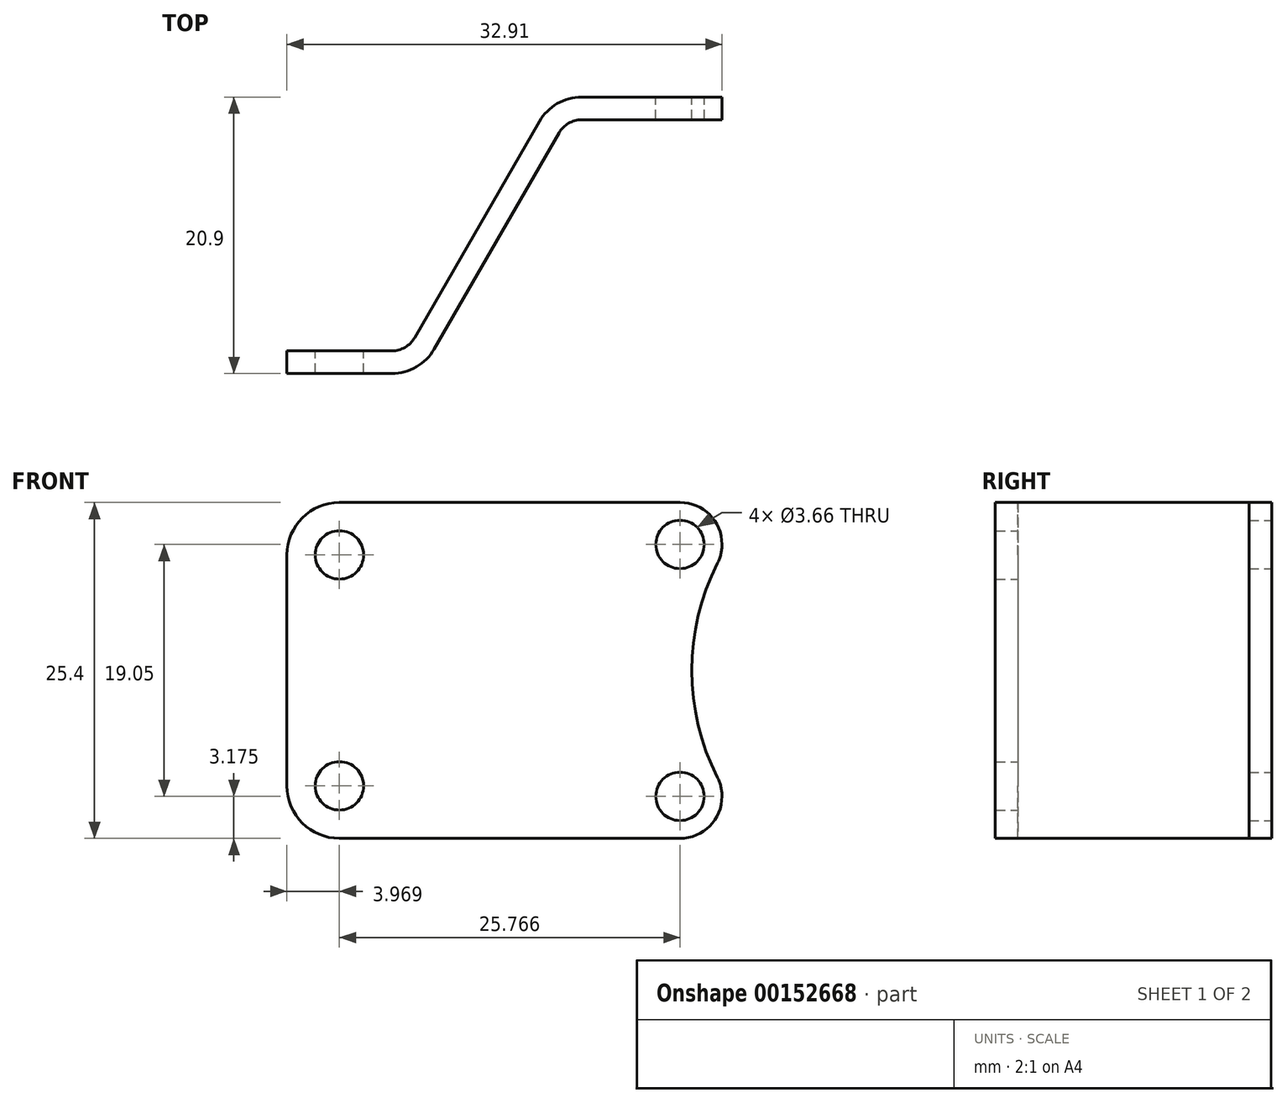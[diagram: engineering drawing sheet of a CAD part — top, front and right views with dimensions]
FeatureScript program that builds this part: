
annotation { "Feature Type Name" : "Feature", "Feature Type Description" : "" }
export const myFeature = defineFeature(function(context is Context, id is Id, definition is map)
    precondition{}
    {
        {
            var Q0;
            Q0=qCreatedBy(makeId("Top.planeOp"),FACE);
            var sketch = newSketch(context, id + "F0", { "sketchPlane" : qUnion([Q0])});
            skLineSegment(sketch, "E0", {"start": v(0, 0) * mm, "end": v(11.08, 19.19) * mm});
            skLineSegment(sketch, "E1", {"start": v(0, 0) * mm, "end": v(-10.07, 0) * mm});
            skLineSegment(sketch, "E2", {"start": v(-10.07, 0) * mm, "end": v(-10.07, 1.7) * mm});
            skLineSegment(sketch, "E3", {"start": v(-10.07, 1.7) * mm, "end": v(-0.99, 1.7) * mm});
            skLineSegment(sketch, "E4", {"start": v(-0.99, 1.7) * mm, "end": v(10.1, 20.9) * mm});
            skLineSegment(sketch, "E5", {"start": v(11.08, 19.19) * mm, "end": v(22.84, 19.19) * mm});
            skLineSegment(sketch, "E6", {"start": v(22.84, 19.19) * mm, "end": v(22.84, 20.9) * mm});
            skLineSegment(sketch, "E7", {"start": v(22.84, 20.9) * mm, "end": v(10.1, 20.9) * mm});
            skLineSegment(sketch, "E8", {"start": v(0, 0) * mm, "end": v(22.84, 0) * mm, "construction": true});
            skLineSegment(sketch, "E9", {"start": v(22.84, 0) * mm, "end": v(22.84, 19.19) * mm, "construction": true});
            skArc(sketch, "E10", {"start": v(-2.13, 1.7) * mm, "mid": v(-1.14, 1.98) * mm, "end": v(-0.41, 2.7) * mm, "construction": true});
            skLineSegment(sketch, "E11", {"start": v(5.54, 9.6) * mm, "end": v(4.06, 10.45) * mm, "construction": true});
            skArc(sketch, "E12", {"start": v(12.22, 19.19) * mm, "mid": v(11.23, 18.92) * mm, "end": v(10.5, 18.2) * mm, "construction": true});
            skSolve(sketch);
        }
        {
            var Q0;
            Q0 = qSketchRegion(id + "F0", true);
            extrude(context, id + "F1", {"entities" : qUnion([Q0]), "depth" : 25.4 * mm});
        }
        {
            var Q0;
            Q0=makeQuery(id+"F1.opExtrude","SWEPT_FACE",FACE,{"disambiguationData":[OSD([sQuery(id+"F0.wireOp",EDGE,"E7")])]});
            var sketch = newSketch(context, id + "F2", { "sketchPlane" : qUnion([Q0])});
            skArc(sketch, "E13", {"start": v(-22.5, 4.61) * mm, "mid": v(-22.75, 3.91) * mm, "end": v(-22.84, 3.18) * mm});
            skArc(sketch, "E14", {"start": v(-22.5, 4.61) * mm, "mid": v(-20.56, 12.7) * mm, "end": v(-22.5, 20.79) * mm});
            skArc(sketch, "E15", {"start": v(-22.84, 22.23) * mm, "mid": v(-22.75, 21.49) * mm, "end": v(-22.5, 20.79) * mm});
            skLineSegment(sketch, "E16", {"start": v(-20.56, 12.7) * mm, "end": v(-22.84, 12.7) * mm, "construction": true});
            skArc(sketch, "E17", {"start": v(-22.5, 20.79) * mm, "mid": v(-16.58, 22.96) * mm, "end": v(-22.84, 22.23) * mm, "construction": true});
            skLineSegment(sketch, "E18", {"start": v(-22.84, 3.18) * mm, "end": v(-22.84, 28.34) * mm});
            skCircle(sketch, "E19", {"center": v(-19.66, 3.18) * mm, "radius": 1.83 * mm});
            skCircle(sketch, "E20", {"center": v(-19.66, 22.23) * mm, "radius": 1.83 * mm});
            skSolve(sketch);
        }
        {
            var Q0;
            Q0 = qSketchRegion(id + "F2", true);
            var Q1;
            Q1=makeQuery(id+"F2.imprint","IMPRINT",FACE,{"disambiguationData":[TD([[makeQuery(id+"F2.imprint","IMPRINT",EDGE,{"derivedFrom":sQuery(id+"F2.wireOp",EDGE,"E13")}),-1.0]])]});
            var Q2;
            Q2=makeQuery(id+"F1.opExtrude","SWEPT_FACE",FACE,{"disambiguationData":[OSD([sQuery(id+"F0.wireOp",EDGE,"E5")])]});
            extrude(context, id + "F3", {"entities" : qUnion([Q0, Q1]), "operationType" : NewBodyOperationType.REMOVE, "endBound" : BoundingType.UP_TO_SURFACE, "oppositeDirection" : true, "endBoundEntityFace" : qUnion([Q2]), "depth" : 25.4 * mm});
        }
        {
            var Q0;
            Q0=makeQuery(id+"F1.opExtrude","SWEPT_EDGE",EDGE,{"disambiguationData":[OSD([sQuery(id+"F0.wireOp",EDGE,"E3"),sQuery(id+"F0.wireOp",EDGE,"E4")])]});
            var Q1;
            Q1=makeQuery(id+"F1.opExtrude","SWEPT_EDGE",EDGE,{"disambiguationData":[OSD([sQuery(id+"F0.wireOp",EDGE,"E0"),sQuery(id+"F0.wireOp",EDGE,"E5")])]});
            fillet(context, id + "F4", {"entities" : qUnion([Q0, Q1]), "radius" : 1.98 * mm, "tangentPropagation" : true, "allowEdgeOverflow" : false});
        }
        {
            var Q0;
            Q0=makeQuery(id+"F1.opExtrude","SWEPT_EDGE",EDGE,{"disambiguationData":[OSD([sQuery(id+"F0.wireOp",EDGE,"E4"),sQuery(id+"F0.wireOp",EDGE,"E7")])]});
            var Q1;
            Q1=makeQuery(id+"F1.opExtrude","SWEPT_EDGE",EDGE,{"disambiguationData":[OSD([sQuery(id+"F0.wireOp",EDGE,"E0"),sQuery(id+"F0.wireOp",EDGE,"E1")])]});
            fillet(context, id + "F5", {"entities" : qUnion([Q0, Q1]), "radius" : 3.7 * mm, "tangentPropagation" : true, "allowEdgeOverflow" : false});
        }
        {
            var Q0;
            Q0=makeQuery(id+"F1.opExtrude","CAP_EDGE",EDGE,{"disambiguationData":[OSD([sQuery(id+"F0.wireOp",EDGE,"E6")])],"isStart":false});
            var Q1;
            Q1=makeQuery(id+"F1.opExtrude","CAP_EDGE",EDGE,{"disambiguationData":[OSD([sQuery(id+"F0.wireOp",EDGE,"E6")])],"isStart":true});
            fillet(context, id + "F6", {"entities" : qUnion([Q0, Q1]), "radius" : 3.17 * mm, "tangentPropagation" : true, "allowEdgeOverflow" : false});
        }
        {
            var Q0;
            Q0=makeQuery(id+"F1.opExtrude","CAP_EDGE",EDGE,{"disambiguationData":[OSD([sQuery(id+"F0.wireOp",EDGE,"E2")])],"isStart":false});
            var Q1;
            Q1=makeQuery(id+"F1.opExtrude","CAP_EDGE",EDGE,{"disambiguationData":[OSD([sQuery(id+"F0.wireOp",EDGE,"E2")])],"isStart":true});
            fillet(context, id + "F7", {"entities" : qUnion([Q0, Q1]), "radius" : 3.97 * mm, "tangentPropagation" : true, "allowEdgeOverflow" : false});
        }
        {
            var Q0;
            Q0=makeQuery(id+"F1.opExtrude","SWEPT_FACE",FACE,{"disambiguationData":[OSD([sQuery(id+"F0.wireOp",EDGE,"E3")])]});
            var sketch = newSketch(context, id + "F8", { "sketchPlane" : qUnion([Q0])});
            skCircle(sketch, "E21", {"center": v(6.1, 3.97) * mm, "radius": 1.83 * mm});
            skCircle(sketch, "E22", {"center": v(6.1, 21.43) * mm, "radius": 1.83 * mm});
            skSolve(sketch);
        }
        {
            var Q0;
            Q0 = qSketchRegion(id + "F8", true);
            var Q1;
            Q1=makeQuery(id+"F1.opExtrude","SWEPT_FACE",FACE,{"disambiguationData":[OSD([sQuery(id+"F0.wireOp",EDGE,"E1")])]});
            extrude(context, id + "F9", {"entities" : qUnion([Q0]), "operationType" : NewBodyOperationType.REMOVE, "endBound" : BoundingType.UP_TO_SURFACE, "oppositeDirection" : true, "endBoundEntityFace" : qUnion([Q1]), "depth" : 25.4 * mm});
        }
    });
